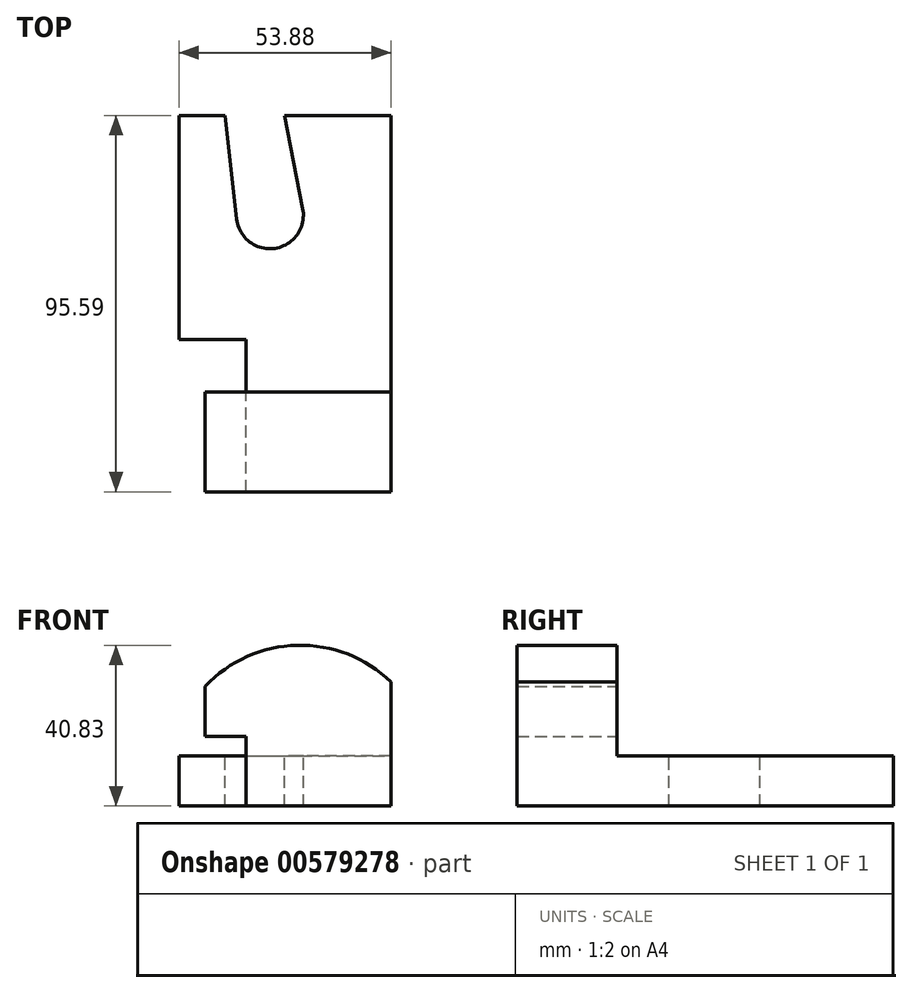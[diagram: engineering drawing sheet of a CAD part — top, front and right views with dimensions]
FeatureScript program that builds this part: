
annotation { "Feature Type Name" : "Feature", "Feature Type Description" : "" }
export const myFeature = defineFeature(function(context is Context, id is Id, definition is map)
    precondition{}
    {
        {
            var Q0;
            Q0=qCreatedBy(makeId("Front.planeOp"),FACE);
            var sketch = newSketch(context, id + "F0", { "sketchPlane" : qUnion([Q0])});
            skArc(sketch, "E0", {"start": v(-11.34, 35.49) * mm, "mid": v(-35.17, 44.79) * mm, "end": v(-58.53, 34.38) * mm});
            skLineSegment(sketch, "E1", {"start": v(-58.53, 34.38) * mm, "end": v(-58.53, 21.66) * mm});
            skLineSegment(sketch, "E2", {"start": v(-11.34, 35.49) * mm, "end": v(-11.34, 21.66) * mm});
            skLineSegment(sketch, "E3", {"start": v(-11.34, 21.66) * mm, "end": v(-11.34, 3.96) * mm});
            skLineSegment(sketch, "E4", {"start": v(-58.53, 21.66) * mm, "end": v(-48.2, 21.66) * mm});
            skLineSegment(sketch, "E5", {"start": v(-48.2, 21.66) * mm, "end": v(-48.2, 3.96) * mm});
            skLineSegment(sketch, "E6", {"start": v(-48.2, 3.96) * mm, "end": v(-11.34, 3.96) * mm});
            skSolve(sketch);
        }
        {
            var Q0;
            Q0=makeQuery(id+"F0.imprint","IMPRINT",FACE,{"disambiguationData":[TD([[makeQuery(id+"F0.imprint","IMPRINT",EDGE,{"derivedFrom":sQuery(id+"F0.wireOp",EDGE,"E0")}),1.0]])]});
            extrude(context, id + "F1", {"entities" : qUnion([Q0]), "depth" : 25.4 * mm, "offsetDistance" : 25.4 * mm});
        }
        {
            var Q0;
            Q0=makeQuery(id+"F1.opExtrude","SWEPT_FACE",FACE,{"disambiguationData":[OSD([sQuery(id+"F0.wireOp",EDGE,"E6")])]});
            var sketch = newSketch(context, id + "F2", { "sketchPlane" : qUnion([Q0])});
            skLineSegment(sketch, "E7.bottom", {"start": v(-11.34, 0) * mm, "end": v(-65.22, 0) * mm});
            skLineSegment(sketch, "E7.top", {"start": v(-11.34, -70.19) * mm, "end": v(-65.22, -70.19) * mm});
            skLineSegment(sketch, "E7.left", {"start": v(-11.34, 0) * mm, "end": v(-11.34, -70.19) * mm});
            skLineSegment(sketch, "E7.right", {"start": v(-65.22, 0) * mm, "end": v(-65.22, -70.19) * mm});
            skSolve(sketch);
        }
        {
            var Q0;
            Q0=makeQuery(id+"F2.imprint","IMPRINT",FACE,{"disambiguationData":[TD([[makeQuery(id+"F2.imprint","IMPRINT",EDGE,{"derivedFrom":sQuery(id+"F2.wireOp",EDGE,"E7.top")}),-1.0]])]});
            extrude(context, id + "F3", {"entities" : qUnion([Q0]), "operationType" : NewBodyOperationType.ADD, "oppositeDirection" : true, "depth" : 12.7 * mm, "offsetDistance" : 25.4 * mm});
        }
        {
            var Q0;
            Q0=makeQuery(id+"F3.opExtrude","CAP_FACE",FACE,{"disambiguationData":[OSD([sQuery(id+"F2.wireOp",EDGE,"E7.bottom"),sQuery(id+"F2.wireOp",EDGE,"E7.top"),sQuery(id+"F2.wireOp",EDGE,"E7.left"),sQuery(id+"F2.wireOp",EDGE,"E7.right")])],"isStart":false});
            var sketch = newSketch(context, id + "F4", { "sketchPlane" : qUnion([Q0])});
            skLineSegment(sketch, "E8.bottom", {"start": v(-48.2, 0) * mm, "end": v(-65.22, 0) * mm});
            skLineSegment(sketch, "E8.top", {"start": v(-48.2, 13.24) * mm, "end": v(-65.22, 13.24) * mm});
            skLineSegment(sketch, "E8.left", {"start": v(-48.2, 0) * mm, "end": v(-48.2, 13.24) * mm});
            skLineSegment(sketch, "E8.right", {"start": v(-65.22, 0) * mm, "end": v(-65.22, 13.24) * mm});
            skSolve(sketch);
        }
        {
            var Q0;
            Q0=makeQuery(id+"F4.imprint","IMPRINT",FACE,{"disambiguationData":[TD([[makeQuery(id+"F4.imprint","IMPRINT",EDGE,{"derivedFrom":sQuery(id+"F4.wireOp",EDGE,"E8.bottom")}),1.0]])]});
            extrude(context, id + "F5", {"entities" : qUnion([Q0]), "operationType" : NewBodyOperationType.REMOVE, "oppositeDirection" : true, "depth" : 25.4 * mm, "offsetDistance" : 25.4 * mm});
        }
        {
            var Q0;
            Q0=makeQuery(id+"F3.opExtrude","CAP_FACE",FACE,{"disambiguationData":[OSD([sQuery(id+"F2.wireOp",EDGE,"E7.bottom"),sQuery(id+"F2.wireOp",EDGE,"E7.top"),sQuery(id+"F2.wireOp",EDGE,"E7.left"),sQuery(id+"F2.wireOp",EDGE,"E7.right")])],"isStart":false});
            var sketch = newSketch(context, id + "F6", { "sketchPlane" : qUnion([Q0])});
            skArc(sketch, "E9", {"start": v(-50.56, 43.89) * mm, "mid": v(-40.8, 36.45) * mm, "end": v(-33.77, 46.5) * mm});
            skLineSegment(sketch, "E10", {"start": v(-33.77, 46.5) * mm, "end": v(-38.45, 70.19) * mm});
            skLineSegment(sketch, "E11", {"start": v(-50.56, 43.89) * mm, "end": v(-53.57, 70.19) * mm});
            skSolve(sketch);
        }
        {
            var Q0;
            Q0=makeQuery(id+"F6.imprint","IMPRINT",FACE,{"disambiguationData":[TD([[makeQuery(id+"F6.imprint","IMPRINT",EDGE,{"derivedFrom":sQuery(id+"F6.wireOp",EDGE,"E9")}),1.0]])]});
            extrude(context, id + "F7", {"entities" : qUnion([Q0]), "operationType" : NewBodyOperationType.REMOVE, "oppositeDirection" : true, "depth" : 25.4 * mm, "offsetDistance" : 25.4 * mm});
        }
    });
